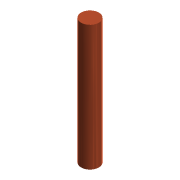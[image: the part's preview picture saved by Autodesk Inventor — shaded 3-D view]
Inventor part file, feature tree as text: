
AUTODESK INVENTOR PART (.ipt)
format: ipt  version: 2016 SP2 (Build 200236200, 236)  size: 78,848 bytes
history: native  units: mm
features: extrude x1, sketch x1
ambient origin geometry x8: Origin, YZ Plane, XZ Plane, XY Plane, X Axis, Y Axis, Z Axis, Center Point
bodies: Body1 (feature_tree)
feature tree (2):
  extrude  "Extrusion3"  Depth=12.0mm TaperAngle=0.0deg
  sketch  "Sketch1"  dims[d4=1.7mm d5=12.0mm d6=0.0mm]
